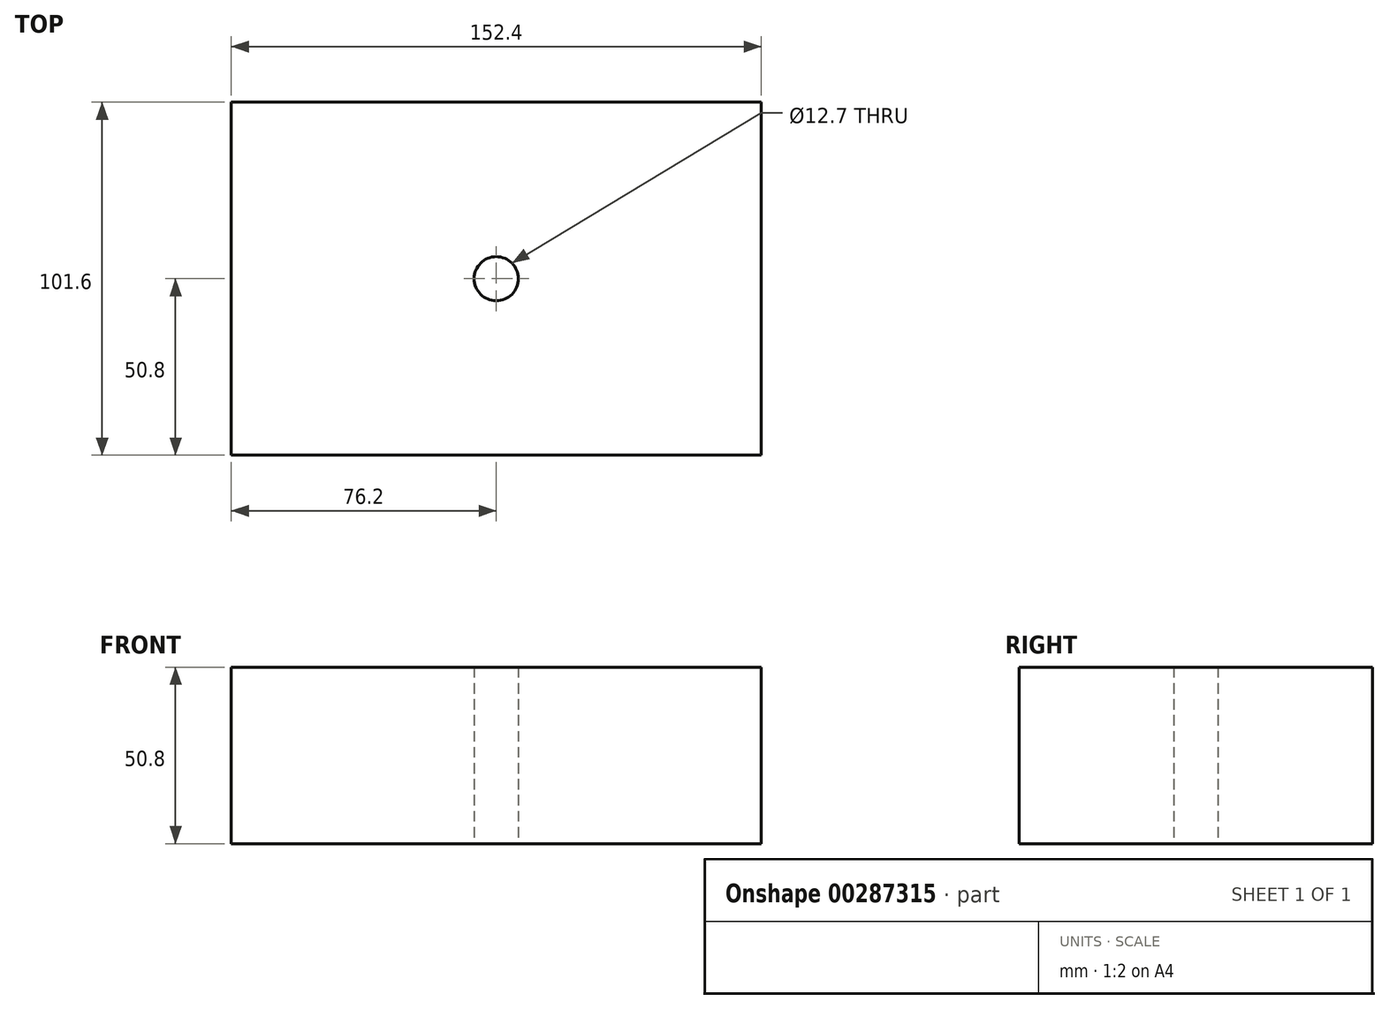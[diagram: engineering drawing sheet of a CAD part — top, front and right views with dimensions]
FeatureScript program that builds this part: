
annotation { "Feature Type Name" : "Feature", "Feature Type Description" : "" }
export const myFeature = defineFeature(function(context is Context, id is Id, definition is map)
    precondition{}
    {
        {
            var Q0;
            Q0=qCreatedBy(makeId("Right.planeOp"),FACE);
            var sketch = newSketch(context, id + "F0", { "sketchPlane" : qUnion([Q0])});
            skLineSegment(sketch, "E0.bottom", {"start": v(0, 0) * mm, "end": v(101.6, 0) * mm});
            skLineSegment(sketch, "E0.top", {"start": v(0, 50.8) * mm, "end": v(101.6, 50.8) * mm});
            skLineSegment(sketch, "E0.left", {"start": v(0, 0) * mm, "end": v(0, 50.8) * mm});
            skLineSegment(sketch, "E0.right", {"start": v(101.6, 0) * mm, "end": v(101.6, 50.8) * mm});
            skSolve(sketch);
        }
        {
            var Q0;
            Q0 = qSketchRegion(id + "F0", true);
            extrude(context, id + "F1", {"entities" : qUnion([Q0]), "depth" : 152.4 * mm});
        }
        {
            var Q0;
            Q0=makeQuery(id+"F1.opExtrude","SWEPT_FACE",FACE,{"disambiguationData":[OSD([sQuery(id+"F0.wireOp",EDGE,"E0.bottom")])]});
            var sketch = newSketch(context, id + "F2", { "sketchPlane" : qUnion([Q0])});
            skCircle(sketch, "E1", {"center": v(76.2, -50.8) * mm, "radius": 6.35 * mm});
            skPoint(sketch, "E1.centerSnap0", {"position": v(76.2, 0) * mm});
            skPoint(sketch, "E1.centerSnap1", {"position": v(0, -50.8) * mm});
            skSolve(sketch);
        }
        {
            var Q0;
            Q0=makeQuery(id+"F2.imprint","IMPRINT",FACE,{"disambiguationData":[TD([[makeQuery(id+"F2.imprint","IMPRINT",EDGE,{"derivedFrom":sQuery(id+"F2.wireOp",EDGE,"E1")}),1.0]])]});
            extrude(context, id + "F3", {"entities" : qUnion([Q0]), "operationType" : NewBodyOperationType.REMOVE, "oppositeDirection" : true, "depth" : 50.8 * mm});
        }
    });
